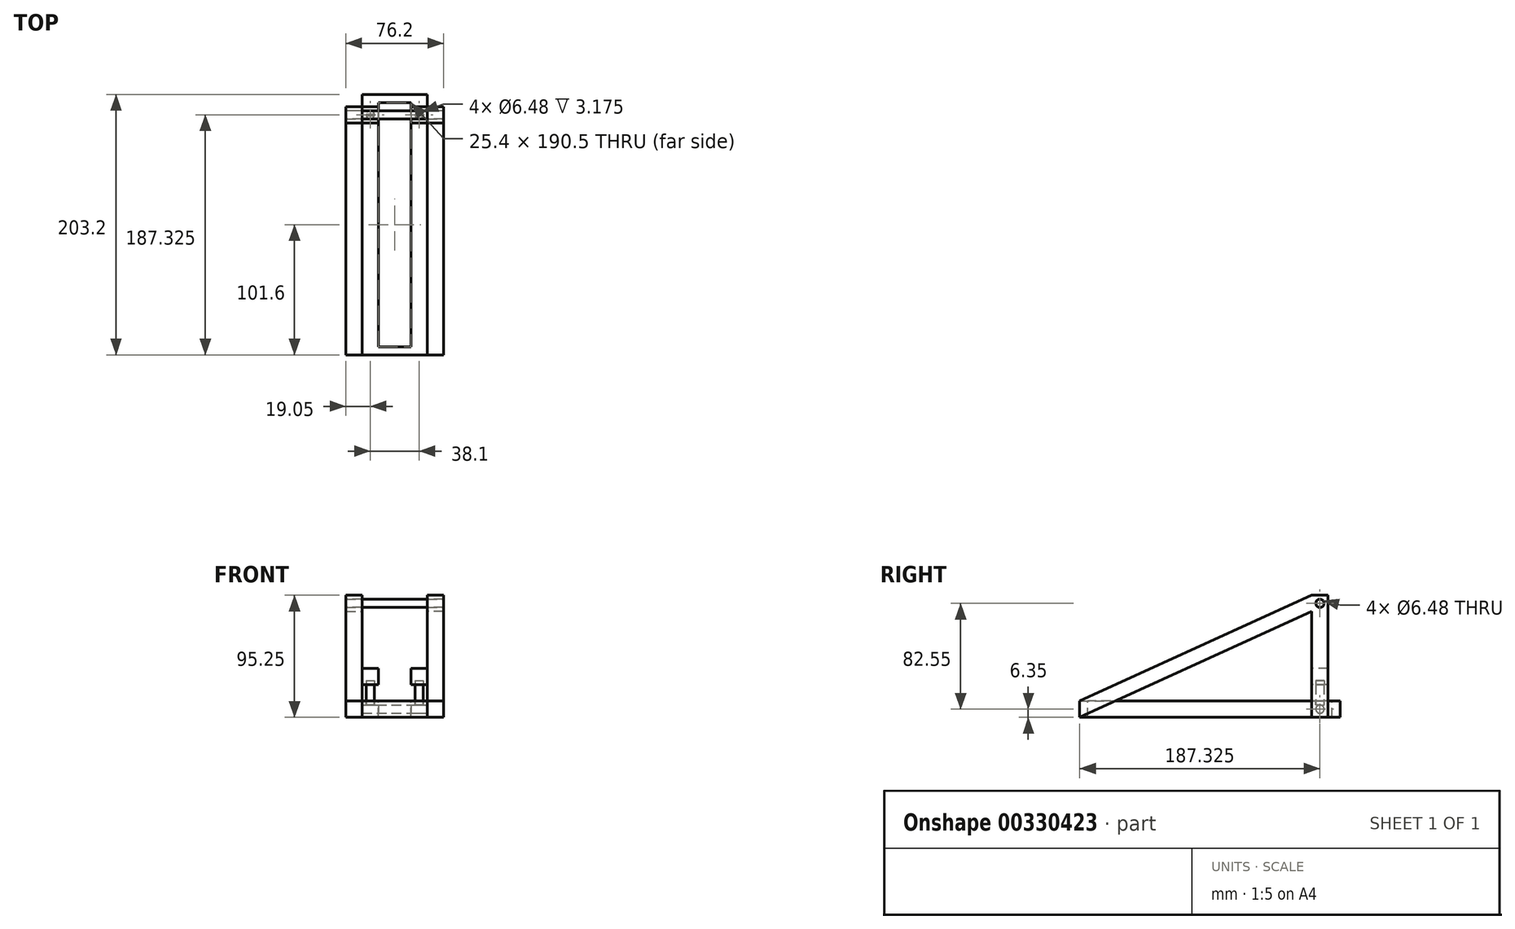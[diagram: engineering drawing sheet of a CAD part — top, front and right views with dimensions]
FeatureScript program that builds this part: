
annotation { "Feature Type Name" : "Feature", "Feature Type Description" : "" }
export const myFeature = defineFeature(function(context is Context, id is Id, definition is map)
    precondition{}
    {
        {
            var Q0;
            Q0=qCreatedBy(makeId("Front.planeOp"),FACE);
            var sketch = newSketch(context, id + "F0", { "sketchPlane" : qUnion([Q0])});
            skLineSegment(sketch, "E0.bottom", {"start": v(0, 0) * mm, "end": v(50.8, 0) * mm});
            skLineSegment(sketch, "E0.top", {"start": v(0, 12.7) * mm, "end": v(50.8, 12.7) * mm});
            skLineSegment(sketch, "E0.left", {"start": v(0, 0) * mm, "end": v(0, 12.7) * mm});
            skLineSegment(sketch, "E0.right", {"start": v(50.8, 0) * mm, "end": v(50.8, 12.7) * mm});
            skSolve(sketch);
        }
        {
            var Q0;
            Q0 = qSketchRegion(id + "F0", true);
            extrude(context, id + "F1", {"entities" : qUnion([Q0]), "depth" : 203.2 * mm});
        }
        {
            var Q0;
            Q0=makeQuery(id+"F1.opExtrude","SWEPT_FACE",FACE,{"disambiguationData":[OSD([sQuery(id+"F0.wireOp",EDGE,"E0.top")])]});
            var sketch = newSketch(context, id + "F2", { "sketchPlane" : qUnion([Q0])});
            skLineSegment(sketch, "E1.bottom", {"start": v(12.7, -6.35) * mm, "end": v(38.1, -6.35) * mm});
            skLineSegment(sketch, "E1.top", {"start": v(12.7, -196.85) * mm, "end": v(38.1, -196.85) * mm});
            skLineSegment(sketch, "E1.left", {"start": v(12.7, -6.35) * mm, "end": v(12.7, -196.85) * mm});
            skLineSegment(sketch, "E1.right", {"start": v(38.1, -6.35) * mm, "end": v(38.1, -196.85) * mm});
            skSolve(sketch);
        }
        {
            var Q0;
            Q0 = qSketchRegion(id + "F2", true);
            extrude(context, id + "F3", {"entities" : qUnion([Q0]), "operationType" : NewBodyOperationType.REMOVE, "endBound" : BoundingType.THROUGH_ALL, "oppositeDirection" : true, "depth" : 12.7 * mm});
        }
        {
            var Q0;
            Q0=makeQuery(id+"F1.opExtrude","SWEPT_FACE",FACE,{"disambiguationData":[OSD([sQuery(id+"F0.wireOp",EDGE,"E0.right")])]});
            var sketch = newSketch(context, id + "F4", { "sketchPlane" : qUnion([Q0])});
            skCircle(sketch, "E2", {"center": v(-15.88, 6.35) * mm, "radius": 3.24 * mm});
            skSolve(sketch);
        }
        {
            var Q0;
            Q0 = qSketchRegion(id + "F4", true);
            extrude(context, id + "F5", {"entities" : qUnion([Q0]), "operationType" : NewBodyOperationType.REMOVE, "endBound" : BoundingType.THROUGH_ALL, "oppositeDirection" : true, "depth" : 25.4 * mm});
        }
        {
            var Q0;
            Q0=makeQuery(id+"F1.opExtrude","SWEPT_FACE",FACE,{"disambiguationData":[OSD([sQuery(id+"F0.wireOp",EDGE,"E0.right")])]});
            var sketch = newSketch(context, id + "F6", { "sketchPlane" : qUnion([Q0])});
            skCircle(sketch, "E3", {"center": v(-15.88, 6.35) * mm, "radius": 3.18 * mm});
            skSolve(sketch);
        }
        {
            var Q0;
            Q0 = qSketchRegion(id + "F6", true);
            extrude(context, id + "F7", {"entities" : qUnion([Q0]), "oppositeDirection" : true, "depth" : 50.8 * mm});
        }
        {
            var Q0;
            Q0=makeQuery(id+"F1.opExtrude","SWEPT_FACE",FACE,{"disambiguationData":[OSD([sQuery(id+"F0.wireOp",EDGE,"E0.right")])]});
            var sketch = newSketch(context, id + "F8", { "sketchPlane" : qUnion([Q0])});
            skLineSegment(sketch, "E4.bottom", {"start": v(-9.53, 0) * mm, "end": v(-22.23, 0) * mm});
            skLineSegment(sketch, "E4.top", {"start": v(-9.53, 95.25) * mm, "end": v(-22.23, 95.25) * mm});
            skLineSegment(sketch, "E4.left", {"start": v(-9.53, 0) * mm, "end": v(-9.53, 95.25) * mm});
            skLineSegment(sketch, "E4.right", {"start": v(-22.23, 0) * mm, "end": v(-22.23, 95.25) * mm});
            skLineSegment(sketch, "E5.left", {"start": v(-203.2, 12.7) * mm, "end": v(-203.2, 0) * mm});
            skLineSegment(sketch, "E6", {"start": v(-203.2, 12.7) * mm, "end": v(-22.22, 95.25) * mm});
            skLineSegment(sketch, "E7", {"start": v(-203.2, 0) * mm, "end": v(-22.22, 82.55) * mm});
            skLineSegment(sketch, "E8", {"start": v(-22.22, 82.55) * mm, "end": v(-22.23, 95.25) * mm});
            skSolve(sketch);
        }
        {
            var Q0;
            Q0 = qSketchRegion(id + "F8", true);
            extrude(context, id + "F9", {"entities" : qUnion([Q0]), "depth" : 12.7 * mm});
        }
        {
            var Q0;
            Q0=makeQuery(id+"F1.opExtrude","SWEPT_FACE",FACE,{"disambiguationData":[OSD([sQuery(id+"F0.wireOp",EDGE,"E0.left")])]});
            var sketch = newSketch(context, id + "F10", { "sketchPlane" : qUnion([Q0])});
            skLineSegment(sketch, "E9.bottom", {"start": v(9.53, 0) * mm, "end": v(22.22, 0) * mm});
            skLineSegment(sketch, "E9.top", {"start": v(9.53, 95.25) * mm, "end": v(22.22, 95.25) * mm});
            skLineSegment(sketch, "E9.left", {"start": v(9.53, 0) * mm, "end": v(9.53, 95.25) * mm});
            skLineSegment(sketch, "E9.right", {"start": v(22.23, 0) * mm, "end": v(22.22, 95.25) * mm});
            skLineSegment(sketch, "E10", {"start": v(22.22, 95.25) * mm, "end": v(203.2, 12.7) * mm});
            skLineSegment(sketch, "E11", {"start": v(203.2, 12.7) * mm, "end": v(203.2, 0) * mm});
            skLineSegment(sketch, "E12", {"start": v(203.2, 0) * mm, "end": v(22.22, 82.55) * mm});
            skLineSegment(sketch, "E13", {"start": v(22.22, 82.55) * mm, "end": v(22.22, 95.25) * mm});
            skLineSegment(sketch, "E14", {"start": v(203.2, 0) * mm, "end": v(203.2, 12.7) * mm});
            skSolve(sketch);
        }
        {
            var Q0;
            Q0 = qSketchRegion(id + "F10", true);
            extrude(context, id + "F11", {"entities" : qUnion([Q0]), "depth" : 12.7 * mm});
        }
        {
            var Q0;
            Q0=makeQuery(id+"F9.opExtrude","CAP_FACE",FACE,{"disambiguationData":[OSD([sQuery(id+"F8.wireOp",EDGE,"E4.bottom"),sQuery(id+"F8.wireOp",EDGE,"E4.top"),sQuery(id+"F8.wireOp",EDGE,"E4.left"),sQuery(id+"F8.wireOp",EDGE,"E4.right")])],"isStart":false});
            var sketch = newSketch(context, id + "F12", { "sketchPlane" : qUnion([Q0])});
            skCircle(sketch, "E15", {"center": v(-15.88, 88.9) * mm, "radius": 3.24 * mm});
            skSolve(sketch);
        }
        {
            var Q0;
            Q0 = qSketchRegion(id + "F12", true);
            extrude(context, id + "F13", {"entities" : qUnion([Q0]), "operationType" : NewBodyOperationType.REMOVE, "endBound" : BoundingType.THROUGH_ALL, "oppositeDirection" : true, "depth" : 76.2 * mm});
        }
        {
            var Q0;
            Q0=makeQuery(id+"F11.opExtrude","CAP_FACE",FACE,{"disambiguationData":[OSD([sQuery(id+"F10.wireOp",EDGE,"E9.bottom"),sQuery(id+"F10.wireOp",EDGE,"E9.top"),sQuery(id+"F10.wireOp",EDGE,"E9.left"),sQuery(id+"F10.wireOp",EDGE,"E9.right")])],"isStart":false});
            var sketch = newSketch(context, id + "F14", { "sketchPlane" : qUnion([Q0])});
            skCircle(sketch, "E16", {"center": v(15.87, 88.9) * mm, "radius": 3.24 * mm});
            skSolve(sketch);
        }
        {
            var Q0;
            Q0 = qSketchRegion(id + "F14", true);
            extrude(context, id + "F15", {"entities" : qUnion([Q0]), "operationType" : NewBodyOperationType.REMOVE, "endBound" : BoundingType.THROUGH_ALL, "oppositeDirection" : true, "depth" : 25.4 * mm});
        }
        {
            var Q0;
            Q0=makeQuery(id+"F11.opExtrude","CAP_FACE",FACE,{"disambiguationData":[OSD([sQuery(id+"F10.wireOp",EDGE,"E9.bottom"),sQuery(id+"F10.wireOp",EDGE,"E9.top"),sQuery(id+"F10.wireOp",EDGE,"E9.left"),sQuery(id+"F10.wireOp",EDGE,"E9.right")])],"isStart":false});
            var sketch = newSketch(context, id + "F16", { "sketchPlane" : qUnion([Q0])});
            skCircle(sketch, "E17", {"center": v(15.87, 88.9) * mm, "radius": 3.18 * mm});
            skSolve(sketch);
        }
        {
            var Q0;
            Q0 = qSketchRegion(id + "F16", true);
            extrude(context, id + "F17", {"entities" : qUnion([Q0]), "oppositeDirection" : true, "depth" : 76.2 * mm});
        }
        {
            var Q0;
            Q0=makeQuery(id+"F1.opExtrude","SWEPT_FACE",FACE,{"disambiguationData":[OSD([sQuery(id+"F0.wireOp",EDGE,"E0.top")])]});
            var sketch = newSketch(context, id + "F18", { "sketchPlane" : qUnion([Q0])});
            skCircle(sketch, "E18", {"center": v(6.35, -15.88) * mm, "radius": 3.24 * mm});
            skCircle(sketch, "E19", {"center": v(44.45, -15.88) * mm, "radius": 3.24 * mm});
            skSolve(sketch);
        }
        {
            var Q0;
            Q0 = qSketchRegion(id + "F18", true);
            extrude(context, id + "F19", {"entities" : qUnion([Q0]), "operationType" : NewBodyOperationType.REMOVE, "oppositeDirection" : true, "depth" : 3.17 * mm});
        }
        {
            var Q0;
            Q0=makeQuery(id+"F1.opExtrude","SWEPT_FACE",FACE,{"disambiguationData":[OSD([sQuery(id+"F0.wireOp",EDGE,"E0.top")])]});
            var sketch = newSketch(context, id + "F20", { "sketchPlane" : qUnion([Q0])});
            skCircle(sketch, "E20", {"center": v(6.35, -15.88) * mm, "radius": 3.18 * mm});
            skCircle(sketch, "E21", {"center": v(44.45, -15.88) * mm, "radius": 3.17 * mm});
            skSolve(sketch);
        }
        {
            var Q0;
            Q0 = qSketchRegion(id + "F20", true);
            extrude(context, id + "F21", {"entities" : qUnion([Q0]), "depth" : 15.88 * mm, "hasSecondDirection" : true, "secondDirectionOppositeDirection" : true, "secondDirectionDepth" : 3.17 * mm});
        }
        {
            var Q0;
            Q0=makeQuery(id+"F11.opExtrude","CAP_FACE",FACE,{"disambiguationData":[OSD([sQuery(id+"F10.wireOp",EDGE,"E9.bottom"),sQuery(id+"F10.wireOp",EDGE,"E9.top"),sQuery(id+"F10.wireOp",EDGE,"E9.left"),sQuery(id+"F10.wireOp",EDGE,"E9.right"),sQuery(id+"F10.wireOp",EDGE,"E10"),sQuery(id+"F10.wireOp",EDGE,"E12"),sQuery(id+"F10.wireOp",EDGE,"E14")])],"isStart":true});
            var sketch = newSketch(context, id + "F22", { "sketchPlane" : qUnion([Q0])});
            skLineSegment(sketch, "E22.bottom", {"start": v(-22.22, 38.1) * mm, "end": v(-9.53, 38.1) * mm});
            skLineSegment(sketch, "E22.top", {"start": v(-22.22, 25.4) * mm, "end": v(-9.53, 25.4) * mm});
            skLineSegment(sketch, "E22.left", {"start": v(-22.22, 38.1) * mm, "end": v(-22.22, 25.4) * mm});
            skLineSegment(sketch, "E22.right", {"start": v(-9.53, 38.1) * mm, "end": v(-9.53, 25.4) * mm});
            skSolve(sketch);
        }
        {
            var Q0;
            Q0 = qSketchRegion(id + "F22", true);
            extrude(context, id + "F23", {"entities" : qUnion([Q0]), "depth" : 12.7 * mm});
        }
        {
            var Q0;
            Q0=makeQuery(id+"F23.opExtrude","SWEPT_FACE",FACE,{"disambiguationData":[OSD([sQuery(id+"F22.wireOp",EDGE,"E22.top")])]});
            var sketch = newSketch(context, id + "F24", { "sketchPlane" : qUnion([Q0])});
            skCircle(sketch, "E23", {"center": v(6.35, 15.87) * mm, "radius": 3.24 * mm});
            skSolve(sketch);
        }
        {
            var Q0;
            Q0 = qSketchRegion(id + "F24", true);
            extrude(context, id + "F25", {"entities" : qUnion([Q0]), "operationType" : NewBodyOperationType.REMOVE, "oppositeDirection" : true, "depth" : 3.17 * mm});
        }
        {
            var Q0;
            Q0=makeQuery(id+"F9.opExtrude","CAP_FACE",FACE,{"disambiguationData":[OSD([sQuery(id+"F8.wireOp",EDGE,"E4.bottom"),sQuery(id+"F8.wireOp",EDGE,"E4.top"),sQuery(id+"F8.wireOp",EDGE,"E4.left"),sQuery(id+"F8.wireOp",EDGE,"E4.right"),sQuery(id+"F8.wireOp",EDGE,"E5.left"),sQuery(id+"F8.wireOp",EDGE,"E6"),sQuery(id+"F8.wireOp",EDGE,"E7")])],"isStart":true});
            var sketch = newSketch(context, id + "F26", { "sketchPlane" : qUnion([Q0])});
            skLineSegment(sketch, "E24.bottom", {"start": v(9.53, 38.1) * mm, "end": v(22.23, 38.1) * mm});
            skLineSegment(sketch, "E24.top", {"start": v(9.53, 25.4) * mm, "end": v(22.23, 25.4) * mm});
            skLineSegment(sketch, "E24.left", {"start": v(9.53, 38.1) * mm, "end": v(9.53, 25.4) * mm});
            skLineSegment(sketch, "E24.right", {"start": v(22.23, 38.1) * mm, "end": v(22.23, 25.4) * mm});
            skSolve(sketch);
        }
        {
            var Q0;
            Q0 = qSketchRegion(id + "F26", true);
            extrude(context, id + "F27", {"entities" : qUnion([Q0]), "operationType" : NewBodyOperationType.ADD, "depth" : 12.7 * mm});
        }
        {
            var Q0;
            Q0=makeQuery(id+"F27.opExtrude","SWEPT_FACE",FACE,{"disambiguationData":[OSD([sQuery(id+"F26.wireOp",EDGE,"E24.top")])]});
            var sketch = newSketch(context, id + "F28", { "sketchPlane" : qUnion([Q0])});
            skCircle(sketch, "E25", {"center": v(44.45, 15.88) * mm, "radius": 3.24 * mm});
            skSolve(sketch);
        }
        {
            var Q0;
            Q0 = qSketchRegion(id + "F28", true);
            extrude(context, id + "F29", {"entities" : qUnion([Q0]), "operationType" : NewBodyOperationType.REMOVE, "oppositeDirection" : true, "depth" : 3.17 * mm});
        }
    });
